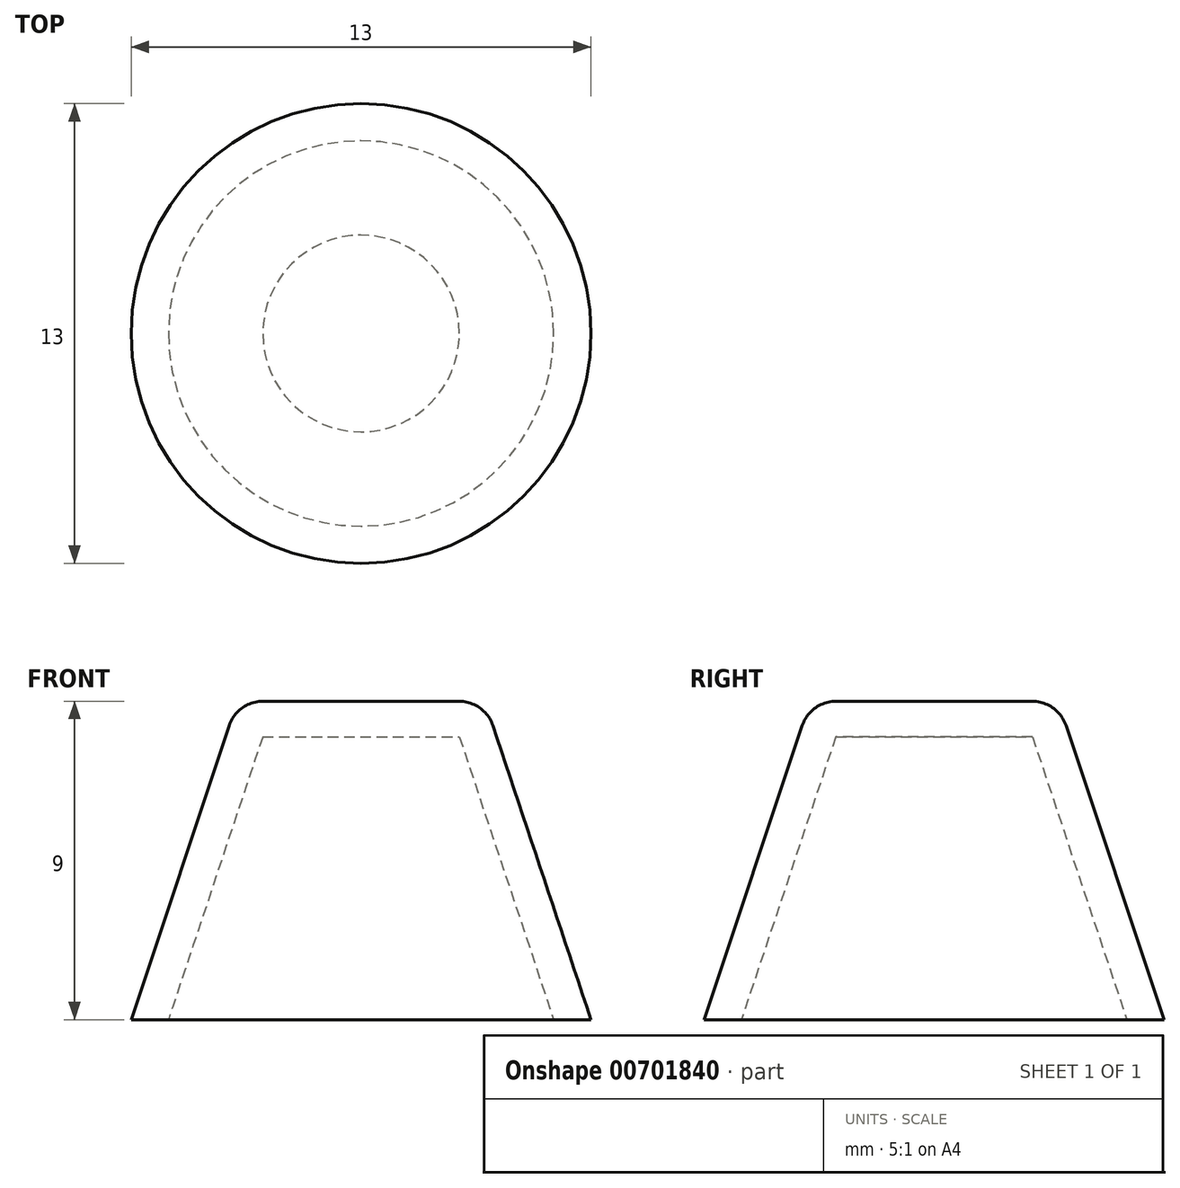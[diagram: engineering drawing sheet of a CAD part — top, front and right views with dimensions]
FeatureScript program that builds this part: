
annotation { "Feature Type Name" : "Feature", "Feature Type Description" : "" }
export const myFeature = defineFeature(function(context is Context, id is Id, definition is map)
    precondition{}
    {
        {
            var Q0;
            Q0=qCreatedBy(makeId("Front.planeOp"),FACE);
            var sketch = newSketch(context, id + "F0", { "sketchPlane" : qUnion([Q0])});
            skLineSegment(sketch, "E0", {"start": v(0, 0) * mm, "end": v(6.5, 0) * mm});
            skLineSegment(sketch, "E1", {"start": v(6.5, 0) * mm, "end": v(3.5, 9) * mm});
            skLineSegment(sketch, "E2", {"start": v(3.5, 9) * mm, "end": v(0, 9) * mm});
            skLineSegment(sketch, "E3", {"start": v(0, 9) * mm, "end": v(0, 0) * mm});
            skSolve(sketch);
        }
        {
            var Q0;
            Q0=makeQuery(id+"F0.imprint","IMPRINT",FACE,{"disambiguationData":[TD([[makeQuery(id+"F0.imprint","IMPRINT",EDGE,{"derivedFrom":sQuery(id+"F0.wireOp",EDGE,"E0")}),1.0]])]});
            var Q1;
            Q1=sQuery(id+"F0.wireOp",EDGE,"E3");
            revolve(context, id + "F1", {"surfaceOperationType" : NewSurfaceOperationType.NEW, "entities" : qUnion([Q0]), "axis" : qUnion([Q1]), "revolveType" : RevolveType.FULL});
        }
        {
            var Q0;
            Q0=makeQuery(id+"F1.opRevolve","SWEPT_FACE",FACE,{"disambiguationData":[OSD([sQuery(id+"F0.wireOp",EDGE,"E0")])]});
            shell(context, id + "F2", {"entities" : qUnion([Q0]), "thickness" : 1 * mm});
        }
        {
            var Q0;
            Q0=makeQuery(id+"F1.opRevolve","SWEPT_EDGE",EDGE,{"disambiguationData":[OSD([sQuery(id+"F0.wireOp",EDGE,"E1"),sQuery(id+"F0.wireOp",EDGE,"E2")])]});
            fillet(context, id + "F3", {"entities" : qUnion([Q0]), "radius" : 1 * mm, "tangentPropagation" : true, "allowEdgeOverflow" : false});
        }
    });
